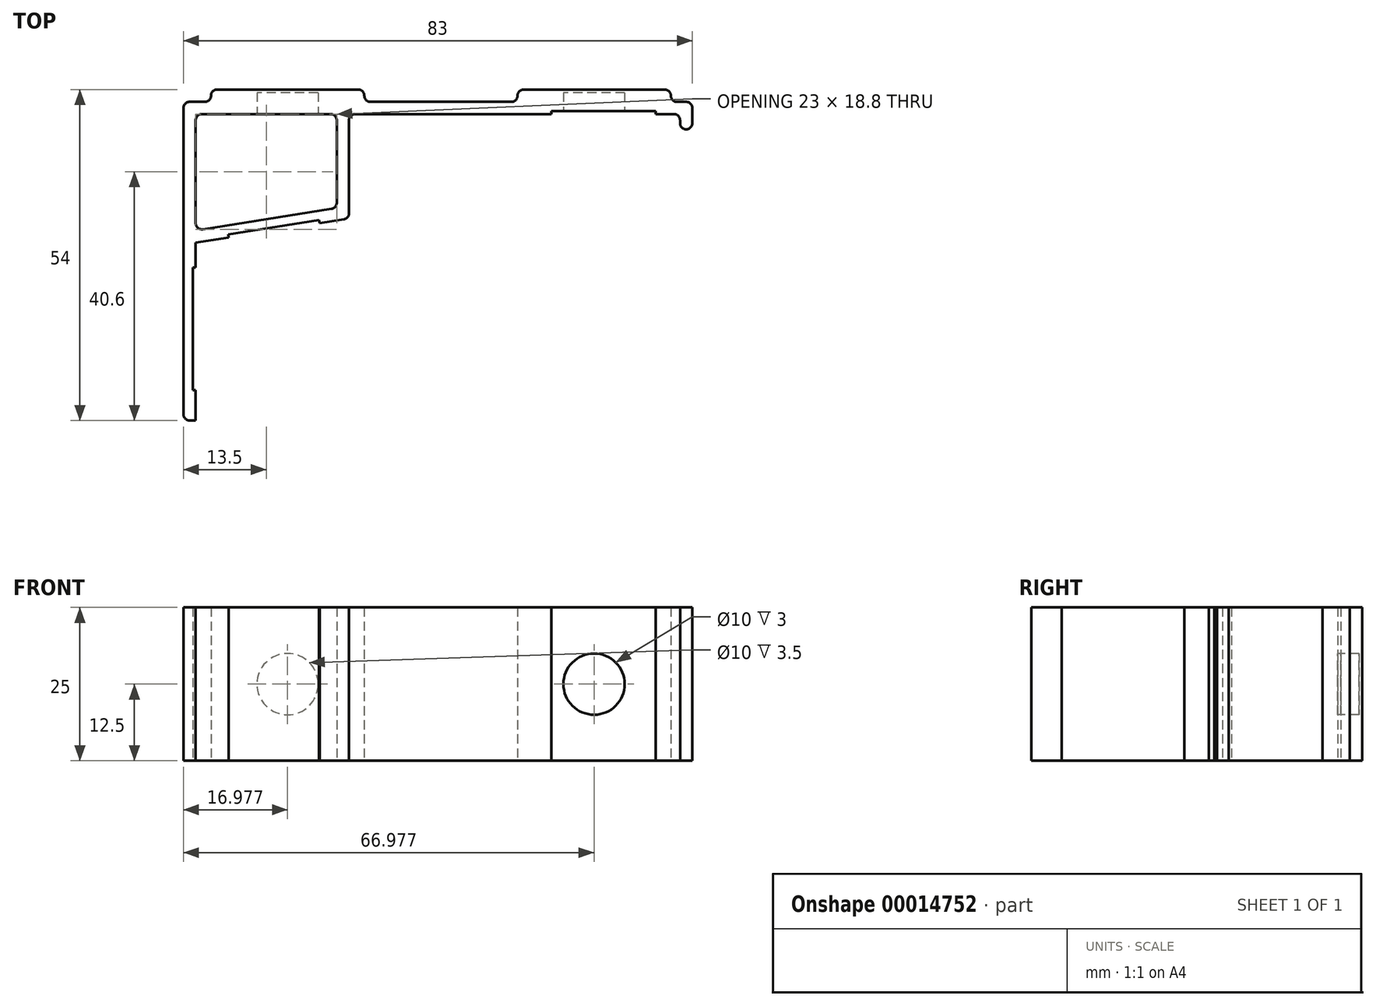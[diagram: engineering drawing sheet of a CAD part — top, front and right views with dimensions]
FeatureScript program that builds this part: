
annotation { "Feature Type Name" : "Feature", "Feature Type Description" : "" }
export const myFeature = defineFeature(function(context is Context, id is Id, definition is map)
    precondition{}
    {
        {
            var Q0;
            Q0=qCreatedBy(makeId("Top.planeOp"),FACE);
            var sketch = newSketch(context, id + "F0", { "sketchPlane" : qUnion([Q0])});
            skLineSegment(sketch, "E0", {"start": v(-10.7, -19.86) * mm, "end": v(-10.7, 30.14) * mm});
            skLineSegment(sketch, "E1", {"start": v(-9.7, 31.14) * mm, "end": v(-7.2, 31.14) * mm});
            skLineSegment(sketch, "E2", {"start": v(72.3, 32.2) * mm, "end": v(72.3, 30.14) * mm});
            skLineSegment(sketch, "E3", {"start": v(69.3, 29.14) * mm, "end": v(17.3, 29.14) * mm});
            skLineSegment(sketch, "E4", {"start": v(-8.7, 28.14) * mm, "end": v(-8.7, 11.34) * mm});
            skLineSegment(sketch, "E5", {"start": v(-8.7, -20.86) * mm, "end": v(-9.7, -20.86) * mm});
            skLineSegment(sketch, "E6", {"start": v(-6.2, 32.14) * mm, "end": v(-6.2, 32.14) * mm});
            skLineSegment(sketch, "E7", {"start": v(-5.2, 33.14) * mm, "end": v(17.8, 33.14) * mm});
            skLineSegment(sketch, "E8", {"start": v(18.8, 32.14) * mm, "end": v(18.8, 32.14) * mm});
            skLineSegment(sketch, "E9", {"start": v(43.8, 32.14) * mm, "end": v(43.8, 32.14) * mm});
            skLineSegment(sketch, "E10", {"start": v(44.8, 33.14) * mm, "end": v(67.8, 33.14) * mm});
            skLineSegment(sketch, "E11", {"start": v(68.8, 32.14) * mm, "end": v(68.8, 32.14) * mm});
            skLineSegment(sketch, "E12", {"start": v(56.3, 41.49) * mm, "end": v(56.3, 25.33) * mm, "construction": true});
            skPoint(sketch, "E12.startSnap0", {"position": v(56.3, 33.14) * mm});
            skLineSegment(sketch, "E13", {"start": v(6.3, 40.27) * mm, "end": v(6.3, 27.15) * mm, "construction": true});
            skPoint(sketch, "E13.startSnap0", {"position": v(6.3, 33.14) * mm});
            skLineSegment(sketch, "E14.trimOffspring", {"start": v(19.8, 31.14) * mm, "end": v(42.8, 31.14) * mm});
            skLineSegment(sketch, "E15.trimOffspring", {"start": v(69.8, 31.14) * mm, "end": v(71.3, 31.14) * mm});
            skPoint(sketch, "E16.visualSharp", {"position": v(-6.2, 33.14) * mm});
            skArc(sketch, "E16.filletArc", {"start": v(-5.2, 33.14) * mm, "mid": v(-5.9, 32.85) * mm, "end": v(-6.2, 32.14) * mm});
            skPoint(sketch, "E17.visualSharp", {"position": v(18.8, 33.14) * mm});
            skArc(sketch, "E17.filletArc", {"start": v(18.8, 32.14) * mm, "mid": v(18.5, 32.85) * mm, "end": v(17.8, 33.14) * mm});
            skPoint(sketch, "E18.visualSharp", {"position": v(-6.2, 31.14) * mm});
            skArc(sketch, "E18.filletArc", {"start": v(-7.2, 31.14) * mm, "mid": v(-6.5, 31.43) * mm, "end": v(-6.2, 32.14) * mm});
            skPoint(sketch, "E19.visualSharp", {"position": v(18.8, 31.14) * mm});
            skArc(sketch, "E19.filletArc", {"start": v(18.8, 32.14) * mm, "mid": v(19.1, 31.43) * mm, "end": v(19.8, 31.14) * mm});
            skPoint(sketch, "E20.visualSharp", {"position": v(-10.7, 31.14) * mm});
            skArc(sketch, "E20.filletArc", {"start": v(-9.7, 31.14) * mm, "mid": v(-10.4, 30.85) * mm, "end": v(-10.7, 30.14) * mm});
            skPoint(sketch, "E21.visualSharp", {"position": v(-8.7, 29.14) * mm});
            skArc(sketch, "E21.filletArc", {"start": v(-7.7, 29.14) * mm, "mid": v(-8.4, 28.85) * mm, "end": v(-8.7, 28.14) * mm});
            skPoint(sketch, "E22.visualSharp", {"position": v(43.8, 33.14) * mm});
            skArc(sketch, "E22.filletArc", {"start": v(44.8, 33.14) * mm, "mid": v(44.1, 32.85) * mm, "end": v(43.8, 32.14) * mm});
            skPoint(sketch, "E23.visualSharp", {"position": v(43.8, 31.14) * mm});
            skArc(sketch, "E23.filletArc", {"start": v(42.8, 31.14) * mm, "mid": v(43.5, 31.43) * mm, "end": v(43.8, 32.14) * mm});
            skPoint(sketch, "E24.visualSharp", {"position": v(68.8, 33.14) * mm});
            skArc(sketch, "E24.filletArc", {"start": v(68.8, 32.14) * mm, "mid": v(68.5, 32.85) * mm, "end": v(67.8, 33.14) * mm});
            skPoint(sketch, "E25.visualSharp", {"position": v(68.8, 31.14) * mm});
            skArc(sketch, "E25.filletArc", {"start": v(68.8, 32.14) * mm, "mid": v(69.1, 31.43) * mm, "end": v(69.8, 31.14) * mm});
            skPoint(sketch, "E26.visualSharp", {"position": v(72.3, 31.14) * mm});
            skArc(sketch, "E26.filletArc", {"start": v(72.3, 30.14) * mm, "mid": v(72, 30.85) * mm, "end": v(71.3, 31.14) * mm});
            skPoint(sketch, "E27.visualSharp", {"position": v(72.3, 29.14) * mm});
            skPoint(sketch, "E28.visualSharp", {"position": v(-10.7, -20.86) * mm});
            skArc(sketch, "E28.filletArc", {"start": v(-10.7, -19.86) * mm, "mid": v(-10.4, -20.57) * mm, "end": v(-9.7, -20.86) * mm});
            skLineSegment(sketch, "E29", {"start": v(-7.72, 8.3) * mm, "end": v(14.3, 11.78) * mm});
            skLineSegment(sketch, "E30", {"start": v(14.3, 14.66) * mm, "end": v(14.3, 28.14) * mm});
            skLineSegment(sketch, "E31", {"start": v(16.3, 28.14) * mm, "end": v(16.3, 14.13) * mm});
            skLineSegment(sketch, "E32", {"start": v(13.46, 13.68) * mm, "end": v(-7.54, 10.35) * mm});
            skLineSegment(sketch, "E33.trimOffspring", {"start": v(13.3, 29.14) * mm, "end": v(-7.7, 29.14) * mm});
            skLineSegment(sketch, "E34.trimOffspring", {"start": v(-8.7, 7.3) * mm, "end": v(-8.7, -20.86) * mm});
            skPoint(sketch, "E35.visualSharp", {"position": v(14.3, 29.14) * mm});
            skArc(sketch, "E35.filletArc", {"start": v(14.3, 28.14) * mm, "mid": v(14, 28.85) * mm, "end": v(13.3, 29.14) * mm});
            skPoint(sketch, "E36.visualSharp", {"position": v(16.3, 29.14) * mm});
            skArc(sketch, "E36.filletArc", {"start": v(17.3, 29.14) * mm, "mid": v(16.6, 28.85) * mm, "end": v(16.3, 28.14) * mm});
            skLineSegment(sketch, "E37", {"start": v(14.3, 11.78) * mm, "end": v(15.46, 11.97) * mm});
            skLineSegment(sketch, "E38", {"start": v(16.3, 12.95) * mm, "end": v(16.3, 14.13) * mm});
            skPoint(sketch, "E39.visualSharp", {"position": v(14.3, 13.8) * mm});
            skArc(sketch, "E39.filletArc", {"start": v(13.46, 13.68) * mm, "mid": v(14.06, 14.01) * mm, "end": v(14.3, 14.66) * mm});
            skPoint(sketch, "E40.visualSharp", {"position": v(16.3, 12.1) * mm});
            skArc(sketch, "E40.filletArc", {"start": v(15.46, 11.97) * mm, "mid": v(16.06, 12.3) * mm, "end": v(16.3, 12.95) * mm});
            skPoint(sketch, "E41.newPointB", {"position": v(-8.7, 8.14) * mm});
            skArc(sketch, "E42.filletArc", {"start": v(-8.7, 11.34) * mm, "mid": v(-8.35, 10.58) * mm, "end": v(-7.54, 10.35) * mm});
            skLineSegment(sketch, "E43", {"start": v(72.3, 30.14) * mm, "end": v(72.3, 27.64) * mm});
            skLineSegment(sketch, "E44", {"start": v(71.3, 26.64) * mm, "end": v(71.3, 26.64) * mm});
            skLineSegment(sketch, "E45", {"start": v(70.3, 27.64) * mm, "end": v(70.3, 28.14) * mm});
            skArc(sketch, "E46.filletArc", {"start": v(70.3, 28.14) * mm, "mid": v(70, 28.85) * mm, "end": v(69.3, 29.14) * mm});
            skPoint(sketch, "E47.visualSharp", {"position": v(70.3, 26.64) * mm});
            skArc(sketch, "E47.filletArc", {"start": v(70.3, 27.64) * mm, "mid": v(70.6, 26.93) * mm, "end": v(71.3, 26.64) * mm});
            skPoint(sketch, "E48.visualSharp", {"position": v(72.3, 26.64) * mm});
            skArc(sketch, "E48.filletArc", {"start": v(71.3, 26.64) * mm, "mid": v(72, 26.93) * mm, "end": v(72.3, 27.64) * mm});
            skLineSegment(sketch, "E49", {"start": v(-7.72, 8.3) * mm, "end": v(-8.7, 8.14) * mm});
            skLineSegment(sketch, "E50", {"start": v(-8.7, 7.3) * mm, "end": v(-8.7, 8.14) * mm});
            skSolve(sketch);
        }
        {
            var Q0;
            Q0=makeQuery(id+"F0.imprint","IMPRINT",FACE,{"disambiguationData":[TD([[makeQuery(id+"F0.imprint","IMPRINT",EDGE,{"derivedFrom":sQuery(id+"F0.wireOp",EDGE,"E0")}),-1.0]])]});
            extrude(context, id + "F1", {"entities" : qUnion([Q0]), "depth" : 25 * mm});
        }
        {
            var Q0;
            Q0=makeQuery(id+"F1.opExtrude","SWEPT_FACE",FACE,{"disambiguationData":[OSD([sQuery(id+"F0.wireOp",EDGE,"E7")])]});
            var sketch = newSketch(context, id + "F2", { "sketchPlane" : qUnion([Q0])});
            skCircle(sketch, "E51", {"center": v(-6.28, 12.5) * mm, "radius": 5 * mm});
            skSolve(sketch);
        }
        {
            var Q0;
            Q0=makeQuery(id+"F1.opExtrude","SWEPT_FACE",FACE,{"disambiguationData":[OSD([sQuery(id+"F0.wireOp",EDGE,"E10")])]});
            var sketch = newSketch(context, id + "F3", { "sketchPlane" : qUnion([Q0])});
            skCircle(sketch, "E52", {"center": v(-56.28, 12.5) * mm, "radius": 5 * mm});
            skSolve(sketch);
        }
        {
            var Q0;
            Q0=makeQuery(id+"F1.opExtrude","SWEPT_FACE",FACE,{"disambiguationData":[OSD([sQuery(id+"F0.wireOp",EDGE,"E34.trimOffspring")])]});
            var sketch = newSketch(context, id + "F4", { "sketchPlane" : qUnion([Q0])});
            skLineSegment(sketch, "E53.bottom", {"start": v(4.1, 25) * mm, "end": v(-15.9, 25) * mm});
            skLineSegment(sketch, "E53.top", {"start": v(4.1, 0) * mm, "end": v(-15.9, 0) * mm});
            skLineSegment(sketch, "E53.left", {"start": v(4.1, 25) * mm, "end": v(4.1, 0) * mm});
            skLineSegment(sketch, "E53.right", {"start": v(-15.9, 25) * mm, "end": v(-15.9, 0) * mm});
            skSolve(sketch);
        }
        {
            var Q0;
            Q0=makeQuery(id+"F4.imprint","IMPRINT",FACE,{"disambiguationData":[TD([[makeQuery(id+"F4.imprint","IMPRINT",EDGE,{"derivedFrom":sQuery(id+"F4.wireOp",EDGE,"E53.bottom")}),1.0]])]});
            extrude(context, id + "F5", {"entities" : qUnion([Q0]), "operationType" : NewBodyOperationType.REMOVE, "oppositeDirection" : true, "depth" : 0.5 * mm});
        }
        {
            var Q0;
            Q0=makeQuery(id+"F1.opExtrude","SWEPT_FACE",FACE,{"disambiguationData":[OSD([sQuery(id+"F0.wireOp",EDGE,"E29"),sQuery(id+"F0.wireOp",EDGE,"E37")])]});
            var sketch = newSketch(context, id + "F6", { "sketchPlane" : qUnion([Q0])});
            skLineSegment(sketch, "E54.bottom", {"start": v(-1.86, 25) * mm, "end": v(13.14, 25) * mm});
            skLineSegment(sketch, "E54.top", {"start": v(-1.86, 0) * mm, "end": v(13.14, 0) * mm});
            skLineSegment(sketch, "E54.left", {"start": v(-1.86, 25) * mm, "end": v(-1.86, 0) * mm});
            skLineSegment(sketch, "E54.right", {"start": v(13.14, 25) * mm, "end": v(13.14, 0) * mm});
            skSolve(sketch);
        }
        {
            var Q0;
            Q0=makeQuery(id+"F1.opExtrude","SWEPT_FACE",FACE,{"disambiguationData":[OSD([sQuery(id+"F0.wireOp",EDGE,"E3")])]});
            var sketch = newSketch(context, id + "F7", { "sketchPlane" : qUnion([Q0])});
            skLineSegment(sketch, "E55.bottom", {"start": v(66.3, 25) * mm, "end": v(49.3, 25) * mm});
            skLineSegment(sketch, "E55.top", {"start": v(66.3, 0) * mm, "end": v(49.3, 0) * mm});
            skLineSegment(sketch, "E55.left", {"start": v(66.3, 25) * mm, "end": v(66.3, 0) * mm});
            skLineSegment(sketch, "E55.right", {"start": v(49.3, 25) * mm, "end": v(49.3, 0) * mm});
            skSolve(sketch);
        }
        {
            var Q0;
            Q0=makeQuery(id+"F7.imprint","IMPRINT",FACE,{"disambiguationData":[TD([[makeQuery(id+"F7.imprint","IMPRINT",EDGE,{"derivedFrom":sQuery(id+"F7.wireOp",EDGE,"E55.bottom")}),1.0]])]});
            extrude(context, id + "F8", {"entities" : qUnion([Q0]), "operationType" : NewBodyOperationType.REMOVE, "oppositeDirection" : true, "depth" : 0.5 * mm});
        }
        {
            var Q0;
            Q0=makeQuery(id+"F6.imprint","IMPRINT",FACE,{"disambiguationData":[TD([[makeQuery(id+"F6.imprint","IMPRINT",EDGE,{"derivedFrom":sQuery(id+"F6.wireOp",EDGE,"E54.bottom")}),1.0]])]});
            extrude(context, id + "F9", {"entities" : qUnion([Q0]), "operationType" : NewBodyOperationType.REMOVE, "oppositeDirection" : true, "depth" : 0.5 * mm});
        }
        {
            var Q0;
            Q0=makeQuery(id+"F8.boolean.opBoolean","COPY",FACE,{"derivedFrom":makeQuery(id+"F8.opExtrude","CAP_FACE",FACE,{"disambiguationData":[OSD([sQuery(id+"F0.wireOp",EDGE,"E3"),sQuery(id+"F3.wireOp",EDGE,"E52"),sQuery(id+"F7.wireOp",EDGE,"E55.bottom"),sQuery(id+"F7.wireOp",EDGE,"E55.top"),sQuery(id+"F7.wireOp",EDGE,"E55.left"),sQuery(id+"F7.wireOp",EDGE,"E55.right")])],"isStart":false})});
            var sketch = newSketch(context, id + "F10", { "sketchPlane" : qUnion([Q0])});
            skCircle(sketch, "E56", {"center": v(56.28, 12.5) * mm, "radius": 5 * mm});
            skSolve(sketch);
        }
        {
            var Q0;
            Q0=makeQuery(id+"F10.imprint","IMPRINT",FACE,{"disambiguationData":[TD([[makeQuery(id+"F10.imprint","IMPRINT",EDGE,{"derivedFrom":sQuery(id+"F10.wireOp",EDGE,"E56")}),1.0]])]});
            var Q1;
            Q1=sQuery(id+"F10.wireOp",EDGE,"E56");
            extrude(context, id + "F11", {"entities" : qUnion([Q0]), "operationType" : NewBodyOperationType.REMOVE, "surfaceEntities" : qUnion([Q1]), "oppositeDirection" : true, "depth" : 3 * mm});
        }
        {
            var Q0;
            Q0=makeQuery(id+"F1.opExtrude","SWEPT_FACE",FACE,{"disambiguationData":[OSD([sQuery(id+"F0.wireOp",EDGE,"E33.trimOffspring")])]});
            var sketch = newSketch(context, id + "F12", { "sketchPlane" : qUnion([Q0])});
            skCircle(sketch, "E57", {"center": v(6.28, 12.5) * mm, "radius": 5 * mm});
            skSolve(sketch);
        }
        {
            var Q0;
            Q0=makeQuery(id+"F12.imprint","IMPRINT",FACE,{"disambiguationData":[TD([[makeQuery(id+"F12.imprint","IMPRINT",EDGE,{"derivedFrom":sQuery(id+"F12.wireOp",EDGE,"E57")}),1.0]])]});
            var Q1;
            Q1=sQuery(id+"F12.wireOp",EDGE,"E57");
            extrude(context, id + "F13", {"entities" : qUnion([Q0]), "operationType" : NewBodyOperationType.REMOVE, "surfaceEntities" : qUnion([Q1]), "oppositeDirection" : true, "depth" : 3.5 * mm});
        }
    });
